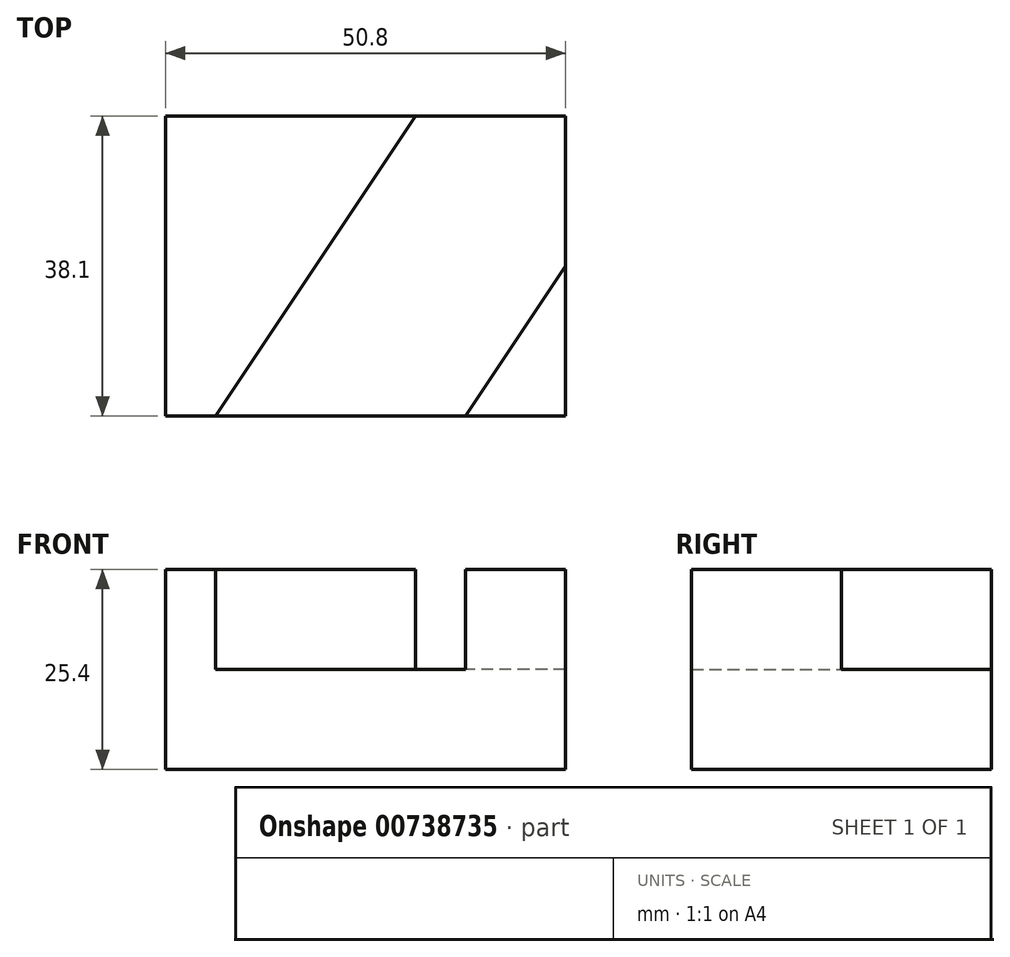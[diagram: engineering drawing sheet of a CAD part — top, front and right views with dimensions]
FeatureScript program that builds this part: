
annotation { "Feature Type Name" : "Feature", "Feature Type Description" : "" }
export const myFeature = defineFeature(function(context is Context, id is Id, definition is map)
    precondition{}
    {
        {
            var Q0;
            Q0=qCreatedBy(makeId("Top.planeOp"),FACE);
            var sketch = newSketch(context, id + "F0", { "sketchPlane" : qUnion([Q0])});
            skLineSegment(sketch, "E0", {"start": v(0, 0) * mm, "end": v(50.8, 0) * mm});
            skLineSegment(sketch, "E1", {"start": v(50.8, 0) * mm, "end": v(50.8, 38.1) * mm});
            skLineSegment(sketch, "E2", {"start": v(50.8, 38.1) * mm, "end": v(0, 38.1) * mm});
            skLineSegment(sketch, "E3", {"start": v(0, 38.1) * mm, "end": v(0, 0) * mm});
            skSolve(sketch);
        }
        {
            var Q0;
            Q0 = qSketchRegion(id + "F0", true);
            extrude(context, id + "F1", {"entities" : qUnion([Q0]), "depth" : 25.4 * mm, "offsetDistance" : 25.4 * mm});
        }
        {
            var Q0;
            Q0=makeQuery(id+"F1.opExtrude","CAP_FACE",FACE,{"disambiguationData":[OSD([sQuery(id+"F0.wireOp",EDGE,"E0"),sQuery(id+"F0.wireOp",EDGE,"E1"),sQuery(id+"F0.wireOp",EDGE,"E2"),sQuery(id+"F0.wireOp",EDGE,"E3")])],"isStart":false});
            var sketch = newSketch(context, id + "F2", { "sketchPlane" : qUnion([Q0])});
            skLineSegment(sketch, "E4", {"start": v(6.35, 0) * mm, "end": v(31.75, 38.1) * mm});
            skLineSegment(sketch, "E5", {"start": v(31.75, 38.1) * mm, "end": v(50.8, 38.1) * mm});
            skLineSegment(sketch, "E6", {"start": v(50.8, 38.1) * mm, "end": v(50.8, 19.05) * mm});
            skLineSegment(sketch, "E7", {"start": v(50.8, 19.05) * mm, "end": v(38.1, 0) * mm});
            skLineSegment(sketch, "E8", {"start": v(38.1, 0) * mm, "end": v(6.35, 0) * mm});
            skSolve(sketch);
        }
        {
            var Q0;
            Q0 = qSketchRegion(id + "F2", true);
            extrude(context, id + "F3", {"entities" : qUnion([Q0]), "operationType" : NewBodyOperationType.REMOVE, "oppositeDirection" : true, "depth" : 12.7 * mm, "offsetDistance" : 25.4 * mm});
        }
    });
